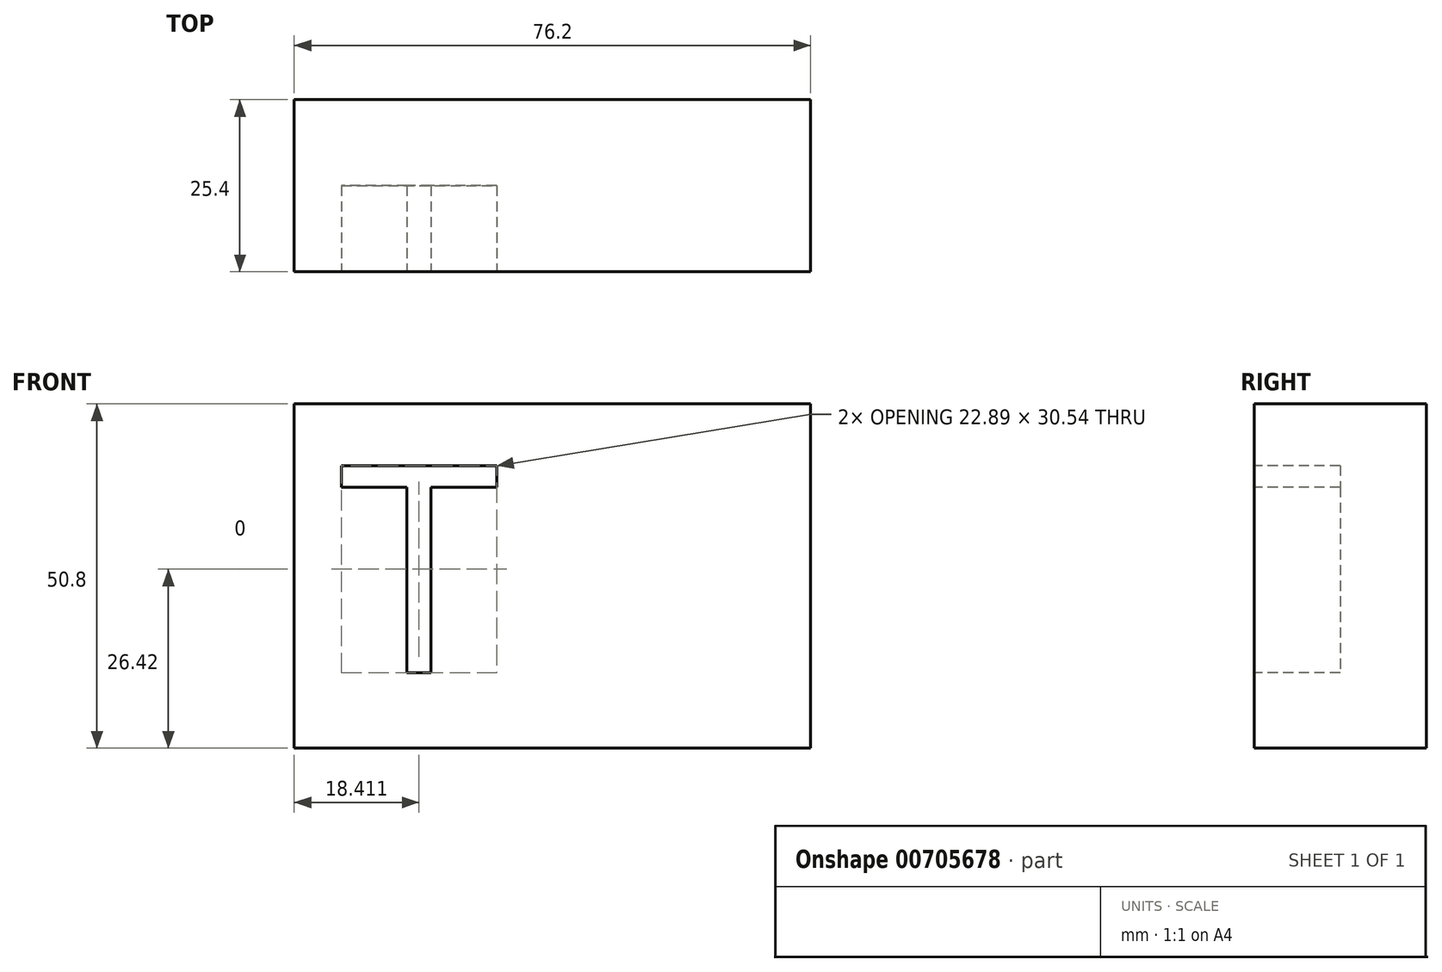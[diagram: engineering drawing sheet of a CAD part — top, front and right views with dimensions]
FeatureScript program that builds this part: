
annotation { "Feature Type Name" : "Feature", "Feature Type Description" : "" }
export const myFeature = defineFeature(function(context is Context, id is Id, definition is map)
    precondition{}
    {
        {
            var Q0;
            Q0=qCreatedBy(makeId("Front.planeOp"),FACE);
            var sketch = newSketch(context, id + "F0", { "sketchPlane" : qUnion([Q0])});
            skLineSegment(sketch, "E0.bottom", {"start": v(-38.1, 25.4) * mm, "end": v(38.1, 25.4) * mm});
            skLineSegment(sketch, "E0.top", {"start": v(-38.1, -25.4) * mm, "end": v(38.1, -25.4) * mm});
            skLineSegment(sketch, "E0.left", {"start": v(-38.1, 25.4) * mm, "end": v(-38.1, -25.4) * mm});
            skLineSegment(sketch, "E0.right", {"start": v(38.1, 25.4) * mm, "end": v(38.1, -25.4) * mm});
            skPoint(sketch, "E0.middle", {"position": v(0, 0) * mm});
            skSolve(sketch);
        }
        {
            var Q0;
            Q0=makeQuery(id+"F0.imprint","IMPRINT",FACE,{"disambiguationData":[TD([[makeQuery(id+"F0.imprint","IMPRINT",EDGE,{"derivedFrom":sQuery(id+"F0.wireOp",EDGE,"E0.bottom")}),-1.0]])]});
            extrude(context, id + "F1", {"entities" : qUnion([Q0]), "depth" : 25.4 * mm, "offsetDistance" : 25.4 * mm});
        }
        {
            var Q0;
            Q0=makeQuery(id+"F1.opExtrude","CAP_FACE",FACE,{"disambiguationData":[OSD([sQuery(id+"F0.wireOp",EDGE,"E0.bottom"),sQuery(id+"F0.wireOp",EDGE,"E0.top"),sQuery(id+"F0.wireOp",EDGE,"E0.left"),sQuery(id+"F0.wireOp",EDGE,"E0.right")])],"isStart":false});
            var sketch = newSketch(context, id + "F2", { "sketchPlane" : qUnion([Q0])});
            skText(sketch, "E1", { "text": "T", "fontName": "OpenSans-Regular.ttf"});
            const initialGuessF2  = {"E1": [-0.03151, -0.01425, 1, 0, 0.0308]};
            skSetInitialGuess(sketch, initialGuessF2);
            skSolve(sketch);
        }
        {
            var Q0;
            Q0=qSketchRegion(id+"F2",true);
            extrude(context, id + "F3", {"entities" : qUnion([Q0]), "operationType" : NewBodyOperationType.REMOVE, "oppositeDirection" : true, "depth" : 12.7 * mm, "offsetDistance" : 25.4 * mm});
        }
    });
